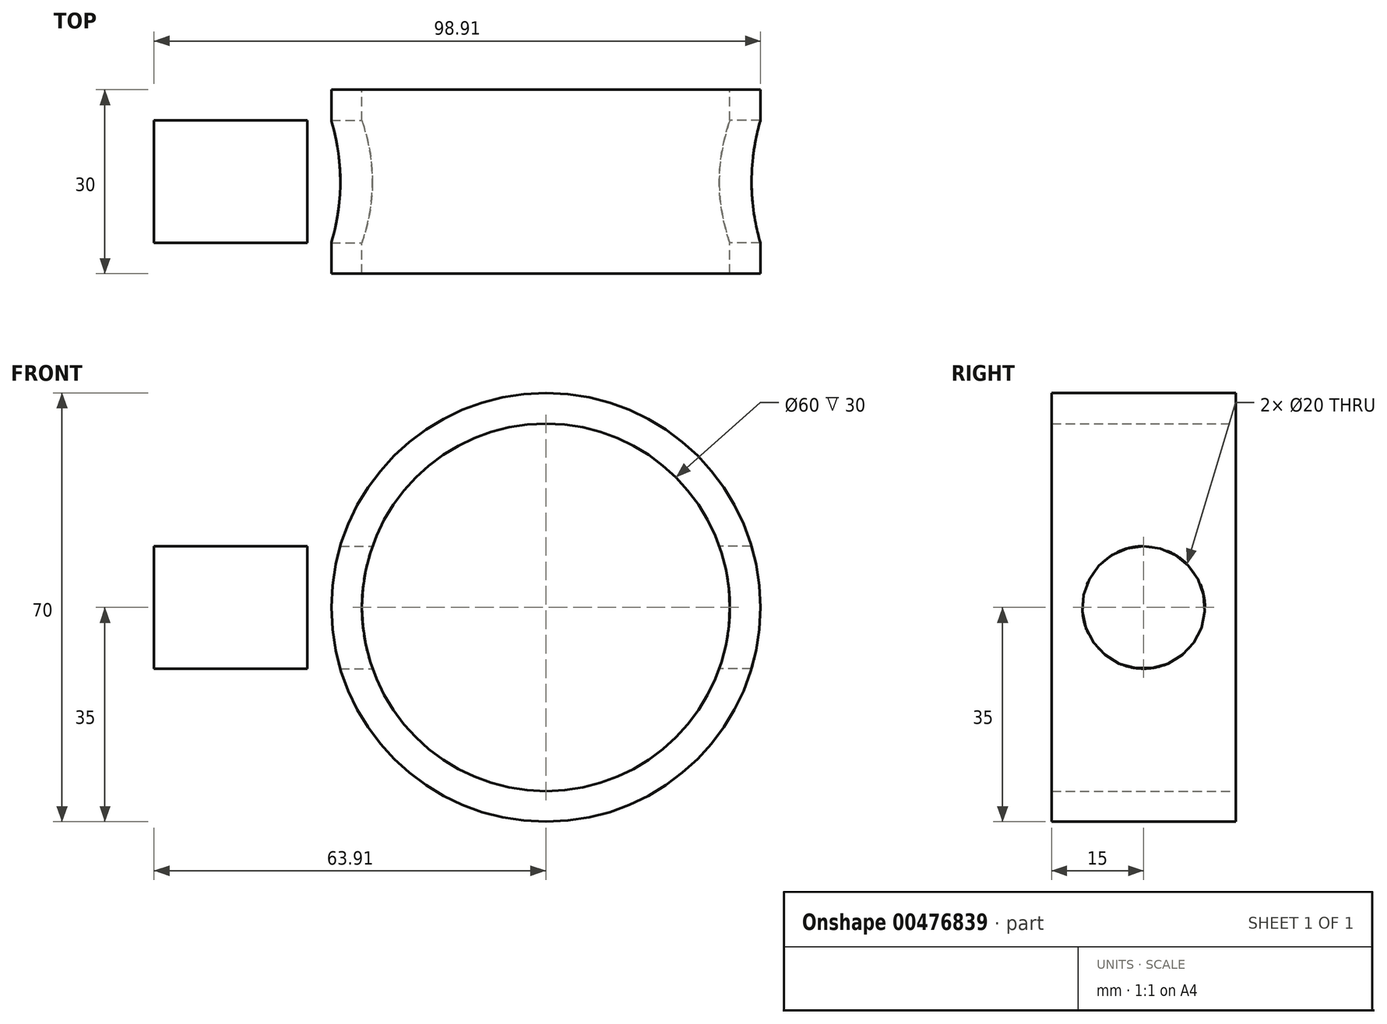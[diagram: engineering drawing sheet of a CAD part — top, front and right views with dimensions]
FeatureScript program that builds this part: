
annotation { "Feature Type Name" : "Feature", "Feature Type Description" : "" }
export const myFeature = defineFeature(function(context is Context, id is Id, definition is map)
    precondition{}
    {
        {
            var Q0;
            Q0=qCreatedBy(makeId("Front.planeOp"),FACE);
            var sketch = newSketch(context, id + "F0", { "sketchPlane" : qUnion([Q0])});
            skCircle(sketch, "E0", {"center": v(0, 0) * mm, "radius": 30 * mm});
            skCircle(sketch, "E1", {"center": v(0, 0) * mm, "radius": 35 * mm});
            skSolve(sketch);
        }
        {
            var Q0;
            Q0=makeQuery(id+"F0.imprint","IMPRINT",FACE,{"disambiguationData":[TD([[makeQuery(id+"F0.imprint","IMPRINT",EDGE,{"derivedFrom":sQuery(id+"F0.wireOp",EDGE,"E0")}),-1.0]])]});
            extrude(context, id + "F1", {"entities" : qUnion([Q0]), "depth" : 30 * mm, "symmetric" : true});
        }
        {
            var Q0;
            Q0=qCreatedBy(makeId("Right.planeOp"),FACE);
            var sketch = newSketch(context, id + "F2", { "sketchPlane" : qUnion([Q0])});
            skCircle(sketch, "E2", {"center": v(0, 0) * mm, "radius": 10 * mm});
            skSolve(sketch);
        }
        {
            var Q0;
            Q0=sQuery(id+"F2.wireOp",VERTEX,"E2.center");
            var Q1;
            Q1=makeQuery(id+"F1.opExtrude","SWEPT_BODY",BODY,{"disambiguationData":[OSD([sQuery(id+"F0.wireOp",EDGE,"E0"),sQuery(id+"F0.wireOp",EDGE,"E1")])]});
            hole(context, id + "F3", {"style" : HoleStyle.SIMPLE, "endStyle" : HoleEndStyle.THROUGH, "holeDiameter" : 20 * mm, "isTappedThrough" : true, "tappedDepth" : 12 * mm, "tapClearance" : 3, "locations" : qUnion([Q0]), "scope" : qUnion([Q1])});
        }
        {
            var Q0;
            Q0=qCreatedBy(makeId("Front.planeOp"),FACE);
            var sketch = newSketch(context, id + "F4", { "sketchPlane" : qUnion([Q0])});
            skLineSegment(sketch, "E3.bottom", {"start": v(-63.9, 0) * mm, "end": v(-38.9, 0) * mm});
            skLineSegment(sketch, "E3.top", {"start": v(-63.9, -10) * mm, "end": v(-38.9, -10) * mm});
            skLineSegment(sketch, "E3.left", {"start": v(-63.9, 0) * mm, "end": v(-63.9, -10) * mm});
            skLineSegment(sketch, "E3.right", {"start": v(-38.9, 0) * mm, "end": v(-38.9, -10) * mm});
            skSolve(sketch);
        }
        {
            var Q0;
            Q0=makeQuery(id+"F4.imprint","IMPRINT",FACE,{"disambiguationData":[TD([[makeQuery(id+"F4.imprint","IMPRINT",EDGE,{"derivedFrom":sQuery(id+"F4.wireOp",EDGE,"E3.bottom")}),-1.0]])]});
            var Q1;
            Q1=sQuery(id+"F4.wireOp",EDGE,"E3.bottom");
            revolve(context, id + "F5", {"entities" : qUnion([Q0]), "axis" : qUnion([Q1]), "revolveType" : RevolveType.FULL});
        }
        {
            var Q0;
            Q0=qCreatedBy(makeId("Right.planeOp"),FACE);
            var sketch = newSketch(context, id + "F6", { "sketchPlane" : qUnion([Q0])});
            skCircle(sketch, "E4", {"center": v(0, 0) * mm, "radius": 10 * mm});
            skSolve(sketch);
        }
        {
            var Q0;
            Q0=sQuery(id+"F6.wireOp",VERTEX,"E4.center");
            var Q1;
            Q1=makeQuery(id+"F1.opExtrude","SWEPT_BODY",BODY,{"disambiguationData":[OSD([sQuery(id+"F0.wireOp",EDGE,"E0"),sQuery(id+"F0.wireOp",EDGE,"E1")])]});
            hole(context, id + "F7", {"style" : HoleStyle.SIMPLE, "endStyle" : HoleEndStyle.THROUGH, "oppositeDirection" : true, "holeDiameter" : 20 * mm, "isTappedThrough" : true, "tappedDepth" : 12 * mm, "tapClearance" : 3, "locations" : qUnion([Q0]), "scope" : qUnion([Q1])});
        }
    });
